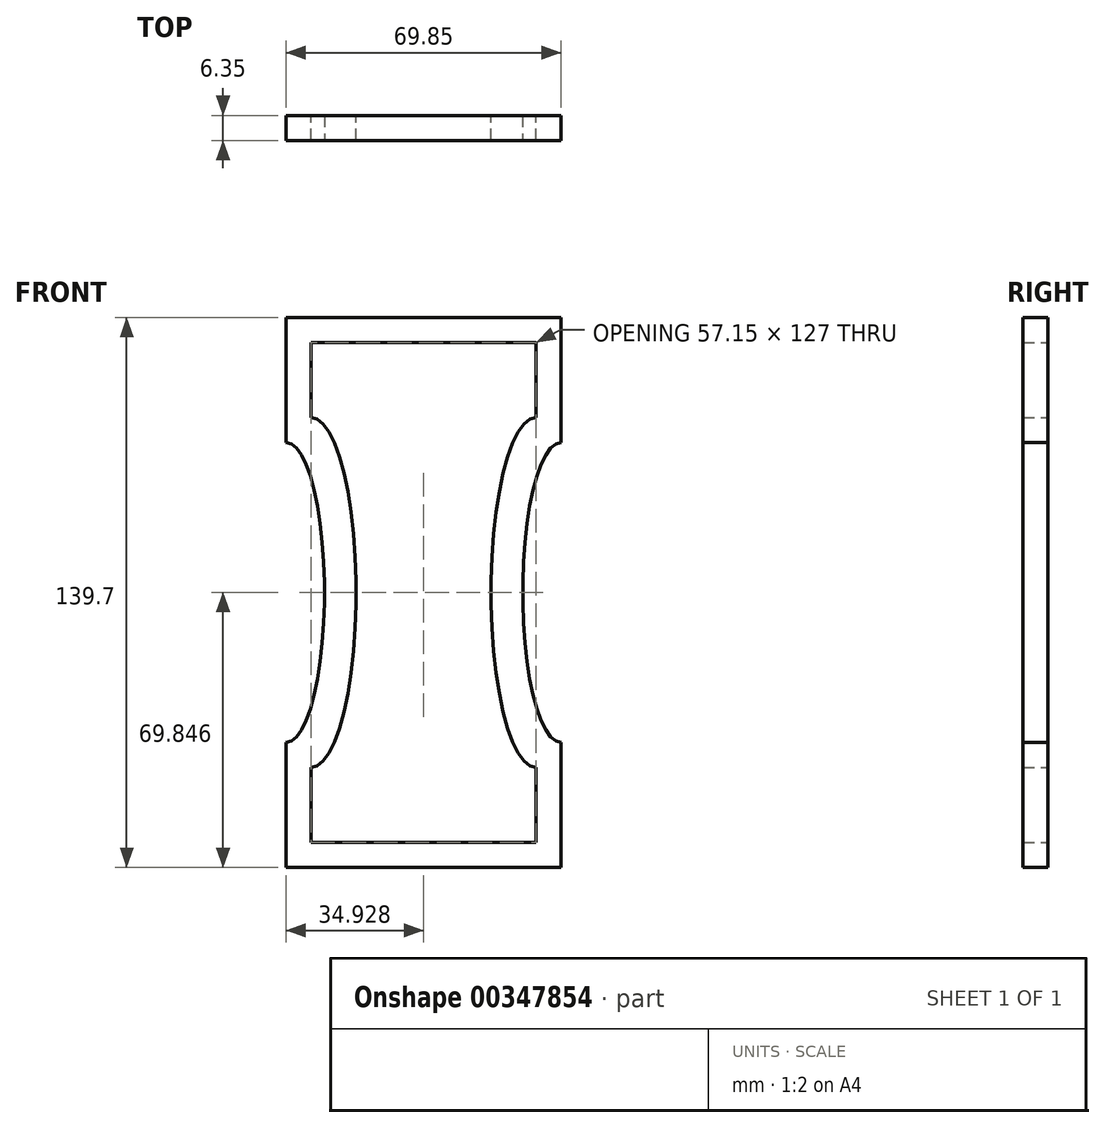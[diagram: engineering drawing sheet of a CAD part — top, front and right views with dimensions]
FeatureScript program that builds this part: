
annotation { "Feature Type Name" : "Feature", "Feature Type Description" : "" }
export const myFeature = defineFeature(function(context is Context, id is Id, definition is map)
    precondition{}
    {
        {
            var Q0;
            Q0=qCreatedBy(makeId("Front.planeOp"),FACE);
            var sketch = newSketch(context, id + "F0", { "sketchPlane" : qUnion([Q0])});
            skLineSegment(sketch, "E0", {"start": v(-72.11, 112.53) * mm, "end": v(-72.11, -68.22) * mm, "construction": true});
            skLineSegment(sketch, "E1", {"start": v(-146, 28.32) * mm, "end": v(-49.89, 28.32) * mm, "construction": true});
            skLineSegment(sketch, "E2", {"start": v(-73.28, 111.76) * mm, "end": v(-73.28, -55.11) * mm, "construction": true});
            skLineSegment(sketch, "E3", {"start": v(-117.73, 28.33) * mm, "end": v(-28.83, 28.33) * mm, "construction": true});
            skLineSegment(sketch, "E4.bottom", {"start": v(-108.2, 98.18) * mm, "end": v(-38.36, 98.18) * mm});
            skPoint(sketch, "E4.middle", {"position": v(-73.28, 28.33) * mm});
            skLineSegment(sketch, "E5.0", {"start": v(-101.86, 91.83) * mm, "end": v(-44.7, 91.83) * mm});
            skLineSegment(sketch, "E6", {"start": v(-101.86, 91.83) * mm, "end": v(-101.86, 72.78) * mm});
            skLineSegment(sketch, "E7.MirrorCS", {"start": v(-101.86, -35.17) * mm, "end": v(-101.86, -16.12) * mm});
            skLineSegment(sketch, "E8.MirrorCS", {"start": v(-44.7, 91.83) * mm, "end": v(-44.7, 72.78) * mm});
            skLineSegment(sketch, "E9.MirrorCS", {"start": v(-44.7, -35.17) * mm, "end": v(-44.7, -16.12) * mm});
            skLineSegment(sketch, "E10", {"start": v(-108.2, 98.18) * mm, "end": v(-108.2, 66.43) * mm});
            skLineSegment(sketch, "E11.MirrorCS", {"start": v(-38.36, 98.18) * mm, "end": v(-38.36, 66.43) * mm});
            skLineSegment(sketch, "E12.MirrorCS", {"start": v(-108.2, -41.52) * mm, "end": v(-108.2, -9.77) * mm});
            skLineSegment(sketch, "E13.MirrorCS", {"start": v(-38.36, -41.52) * mm, "end": v(-38.36, -9.77) * mm});
            skPoint(sketch, "E14.orphan", {"position": v(-108.2, -41.52) * mm});
            skPoint(sketch, "E4.top.end.orphan", {"position": v(-38.36, -41.52) * mm});
            skLineSegment(sketch, "E15.MirrorCS", {"start": v(-101.86, -35.17) * mm, "end": v(-44.7, -35.17) * mm});
            skLineSegment(sketch, "E16.MirrorCS", {"start": v(-108.2, -41.52) * mm, "end": v(-38.36, -41.52) * mm});
            skLineSegment(sketch, "E17", {"start": v(-108.2, 66.43) * mm, "end": v(-108.2, -9.77) * mm, "construction": true});
            skLineSegment(sketch, "E18", {"start": v(-101.86, 72.78) * mm, "end": v(-101.86, -16.12) * mm, "construction": true});
            skEllipticalArc(sketch, "E19", {});
            skEllipticalArc(sketch, "E20", {});
            skEllipticalArc(sketch, "E21.trimOffspring", {});
            skEllipticalArc(sketch, "E22.trimOffspring", {});
            skEllipticalArc(sketch, "E23.MirrorCS", {});
            skEllipticalArc(sketch, "E24.MirrorCS", {});
            const initialGuessF0  = {"E19": [-0.1082065626978874, 0.028326360887289057, 0, 1, 0.0381, 0.009747932984064105, 3.141592653589793, 0], "E20": [-0.10185656269788741, 0.028326360887289057, 0, 1, 0.04445, 0.011425213810996485, 2.5522817580940105, 2.5987378353244415], "E21.trimOffspring": [-0.10185656269788741, 0.028326360887289057, 0, 1, 0.04445, 0.011425213810996485, 0.5428548182653519, 0.5893108954957829], "E22.trimOffspring": [-0.10185656269788741, 0.028326360887289057, 0, 1, 0.04445, 0.011425213810996485, 3.141592653589793, 0], "E23.MirrorCS": [-0.044706562697887406, 0.02832636088728907, 0, 1, 0.04445, 0.011425213810996485, 0, 3.141592653589793], "E24.MirrorCS": [-0.038356562697887404, 0.02832636088728907, 0, 1, 0.0381, 0.009747932984064105, 0, 3.141592653589793]};
            skSetInitialGuess(sketch, initialGuessF0);
            skSolve(sketch);
        }
        {
            var Q0;
            Q0 = qSketchRegion(id + "F0", true);
            extrude(context, id + "F1", {"entities" : qUnion([Q0]), "flatOperationType" : FlatOperationType.REMOVE, "offsetDistance" : 25.4 * mm, "depth" : 6.35 * mm, "domain" : OperationDomain.MODEL});
        }
    });
